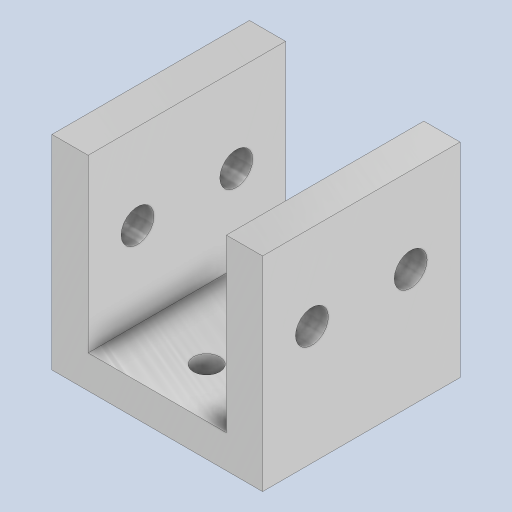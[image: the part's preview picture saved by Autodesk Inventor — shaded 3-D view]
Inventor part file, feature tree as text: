
AUTODESK INVENTOR PART (.ipt)
format: ipt  version: 2023 (Build 270158000, 158)  size: 267,264 bytes
history: native  units: mm
features: sketch x3, extrude x2, hole x2
ambient origin geometry x8: Origin, YZ Plane, XZ Plane, XY Plane, X Axis, Y Axis, Z Axis, Center Point
bodies: Body1 (feature_tree)
feature tree (7):
  extrude  "Extrusion1"  Depth=30.0mm
  extrude  "Extrusion2"  Depth=5.5mm
  hole  "Hole2"  [1 undecoded]
  hole  "Furo3"  [1 undecoded]
  sketch  "Esboço1"  dims[d0=32.0mm d1=30.0mm]
  sketch  "Sketch4"  dims[d24=5.0mm d25=0.0mm d26=5.5mm]
  sketch  "Sketch5"  dims[d27=5.5mm d28=26.0mm d29=0.0mm d30=7.5mm d31=7.5mm d32=13.0mm d33=13.0mm d34=5.0mm d35=6.0mm d36=4.0mm d37=2.0mm d38=90.0deg d39=5.0mm d40=20.594885mm d43=15.0mm d45=21.0mm d48=30.0mm d50=4.0mm d51=6.0mm d52=7.0mm d53=3.0mm d54=90.0deg d55=5.0mm d56=20.594885mm d57=10.5mm d58=7.5mm d59=0.5mm d60=0.872665mm]
note: 2 required parameter values undecoded (feature->parameter linkage not recoverable at this tier; creation-order binding heuristic only, values carry confidence <= 0.55)
